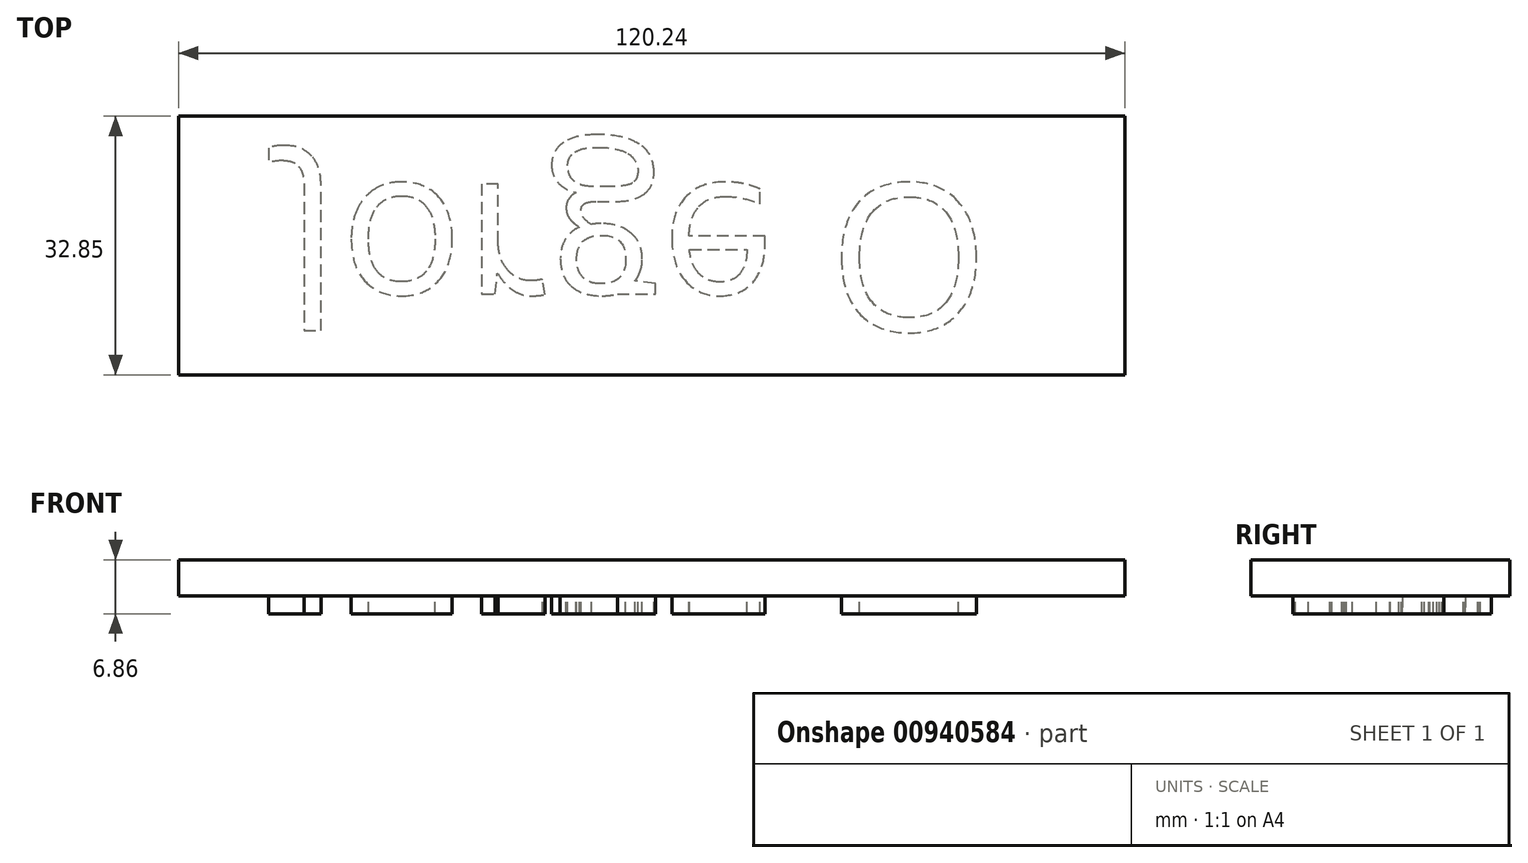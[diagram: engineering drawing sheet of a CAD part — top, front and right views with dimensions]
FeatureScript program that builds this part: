
annotation { "Feature Type Name" : "Feature", "Feature Type Description" : "" }
export const myFeature = defineFeature(function(context is Context, id is Id, definition is map)
    precondition{}
    {
        {
            var Q0;
            Q0=qCreatedBy(makeId("Top.planeOp"),FACE);
            var sketch = newSketch(context, id + "F0", { "sketchPlane" : qUnion([Q0])});
            skLineSegment(sketch, "E0.bottom", {"start": v(-50.8, -5.86) * mm, "end": v(69.43, -5.86) * mm});
            skLineSegment(sketch, "E0.top", {"start": v(-50.8, -38.7) * mm, "end": v(69.43, -38.7) * mm});
            skLineSegment(sketch, "E0.left", {"start": v(-50.8, -5.86) * mm, "end": v(-50.8, -38.7) * mm});
            skLineSegment(sketch, "E0.right", {"start": v(69.43, -5.86) * mm, "end": v(69.43, -38.7) * mm});
            skSolve(sketch);
        }
        {
            var Q0;
            Q0=makeQuery(id+"F0.imprint","IMPRINT",FACE,{"disambiguationData":[TD([[makeQuery(id+"F0.imprint","IMPRINT",EDGE,{"derivedFrom":sQuery(id+"F0.wireOp",EDGE,"E0.bottom")}),-1.0]])]});
            extrude(context, id + "F1", {"entities" : qUnion([Q0]), "oppositeDirection" : true, "depth" : 4.57 * mm, "offsetDistance" : 25.4 * mm});
        }
        {
            var Q0;
            Q0=makeQuery(id+"F1.opExtrude","CAP_FACE",FACE,{"disambiguationData":[OSD([sQuery(id+"F0.wireOp",EDGE,"E0.bottom"),sQuery(id+"F0.wireOp",EDGE,"E0.top"),sQuery(id+"F0.wireOp",EDGE,"E0.left"),sQuery(id+"F0.wireOp",EDGE,"E0.right")])],"isStart":false});
            var sketch = newSketch(context, id + "F2", { "sketchPlane" : qUnion([Q0])});
            skText(sketch, "E1", { "text": "Jorge O", "fontName": "OpenSans-Regular.ttf"});
            const initialGuessF2  = {"E1": [-0.0373, 0.01447, 1, 0, 0.01879]};
            skSetInitialGuess(sketch, initialGuessF2);
            skSolve(sketch);
        }
        {
            var Q0;
            Q0 = qSketchRegion(id + "F2", true);
            extrude(context, id + "F3", {"entities" : qUnion([Q0]), "operationType" : NewBodyOperationType.ADD, "depth" : 2.3 * mm, "offsetDistance" : 25.4 * mm});
        }
    });
